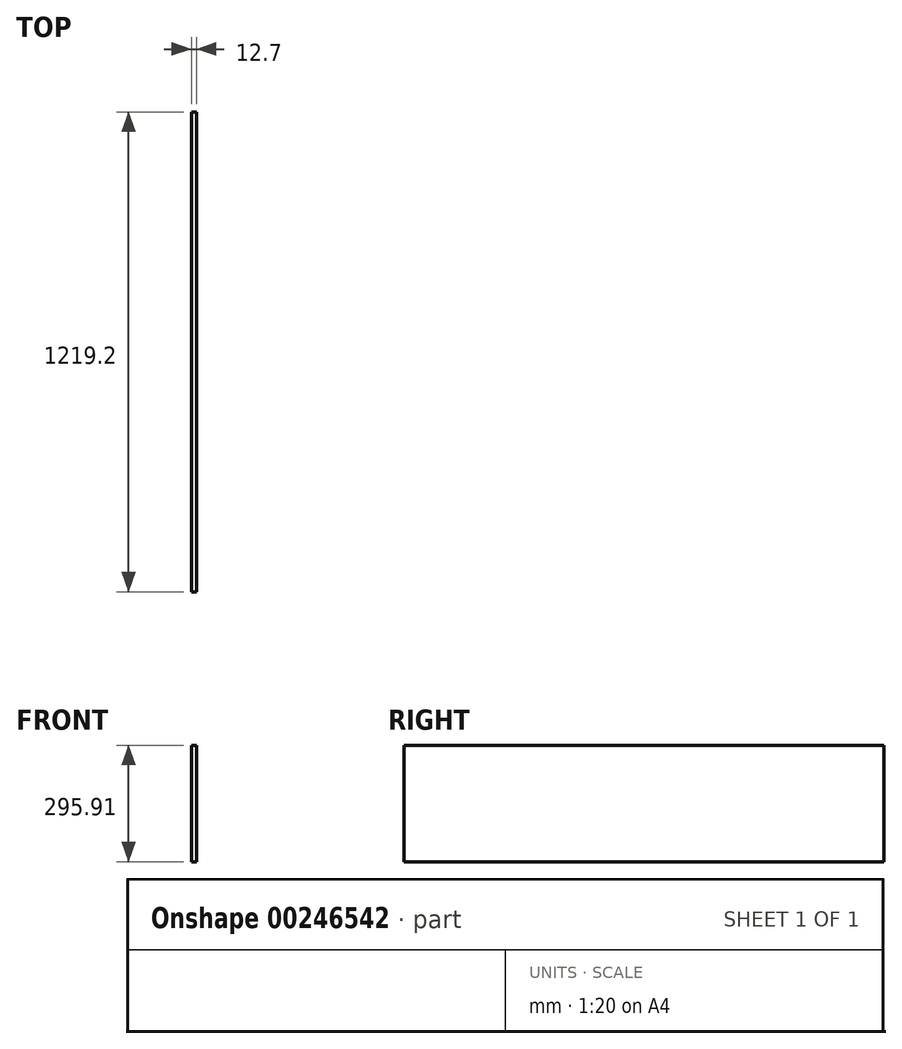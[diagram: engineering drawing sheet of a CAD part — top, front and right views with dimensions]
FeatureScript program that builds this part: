
annotation { "Feature Type Name" : "Feature", "Feature Type Description" : "" }
export const myFeature = defineFeature(function(context is Context, id is Id, definition is map)
    precondition{}
    {
        {
            var Q0;
            Q0=qCreatedBy(makeId("Right.planeOp"),FACE);
            var sketch = newSketch(context, id + "F0", { "sketchPlane" : qUnion([Q0])});
            skLineSegment(sketch, "E0.bottom", {"start": v(0, 0) * mm, "end": v(-1219.2, 0) * mm});
            skLineSegment(sketch, "E0.top", {"start": v(0, 295.91) * mm, "end": v(-1219.2, 295.91) * mm});
            skLineSegment(sketch, "E0.left", {"start": v(0, 0) * mm, "end": v(0, 295.9) * mm});
            skLineSegment(sketch, "E0.right", {"start": v(-1219.2, 0) * mm, "end": v(-1219.2, 295.91) * mm});
            skSolve(sketch);
        }
        {
            var Q0;
            Q0=makeQuery(id+"F0.imprint","IMPRINT",FACE,{"disambiguationData":[TD([[makeQuery(id+"F0.imprint","IMPRINT",EDGE,{"derivedFrom":sQuery(id+"F0.wireOp",EDGE,"E0.bottom")}),-1.0]])]});
            extrude(context, id + "F1", {"entities" : qUnion([Q0]), "depth" : 12.7 * mm});
        }
    });
